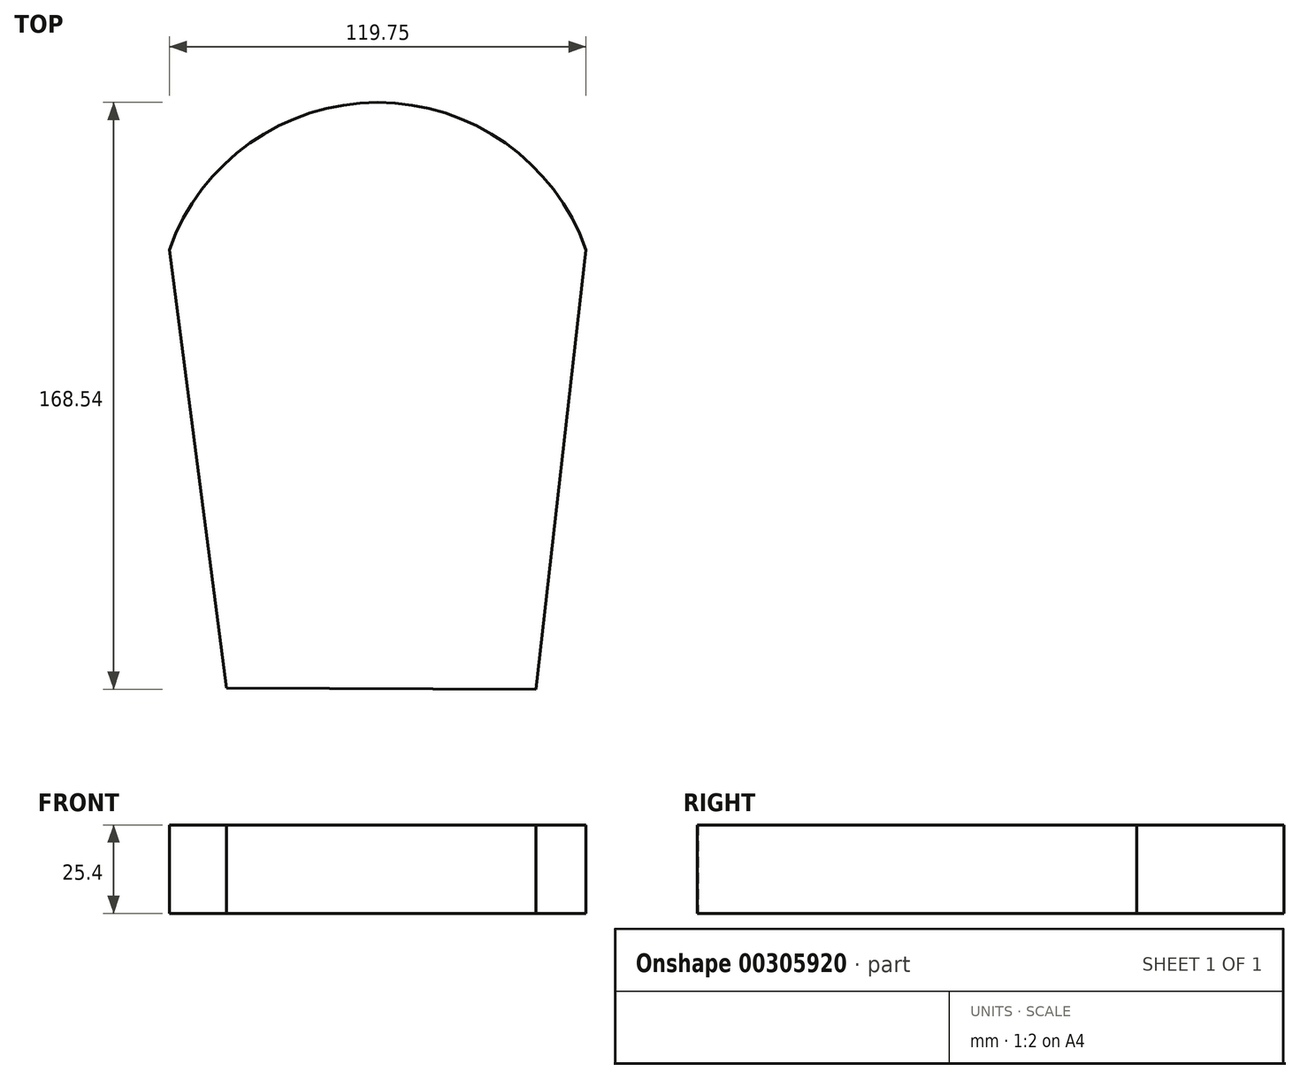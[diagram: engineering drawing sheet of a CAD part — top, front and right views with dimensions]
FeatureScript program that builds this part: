
annotation { "Feature Type Name" : "Feature", "Feature Type Description" : "" }
export const myFeature = defineFeature(function(context is Context, id is Id, definition is map)
    precondition{}
    {
        {
            var Q0;
            Q0=qCreatedBy(makeId("Top.planeOp"),FACE);
            var sketch = newSketch(context, id + "F0", { "sketchPlane" : qUnion([Q0])});
            skArc(sketch, "E0", {"start": v(119.75, 0) * mm, "mid": v(59.87, 42.35) * mm, "end": v(0, 0) * mm});
            skLineSegment(sketch, "E1", {"start": v(0, 0) * mm, "end": v(16.5, -125.92) * mm});
            skLineSegment(sketch, "E2", {"start": v(16.5, -125.92) * mm, "end": v(105.4, -126.19) * mm});
            skLineSegment(sketch, "E3", {"start": v(119.75, 0) * mm, "end": v(105.4, -126.19) * mm});
            skSolve(sketch);
        }
        {
            var Q0;
            Q0 = qSketchRegion(id + "F0", true);
            extrude(context, id + "F1", {"entities" : qUnion([Q0]), "depth" : 25.4 * mm});
        }
    });
